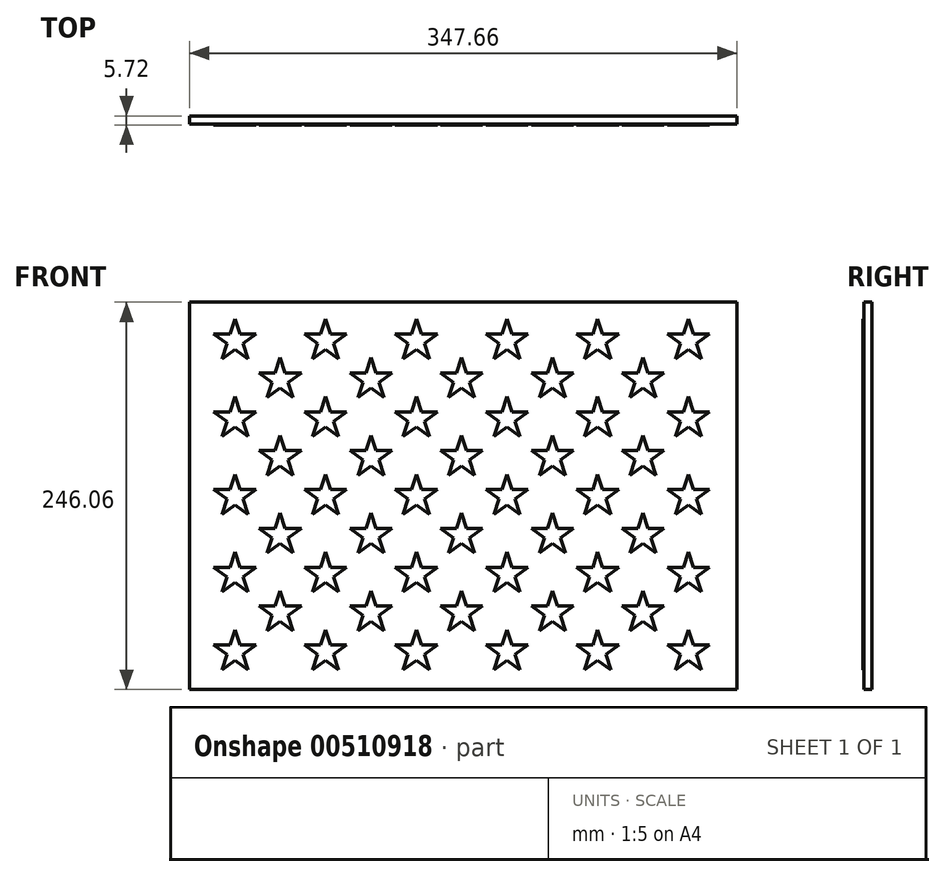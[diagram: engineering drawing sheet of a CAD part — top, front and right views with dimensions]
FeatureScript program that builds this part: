
annotation { "Feature Type Name" : "Feature", "Feature Type Description" : "" }
export const myFeature = defineFeature(function(context is Context, id is Id, definition is map)
    precondition{}
    {
        {
            var Q0;
            Q0=qCreatedBy(makeId("Front.planeOp"),FACE);
            var sketch = newSketch(context, id + "F0", { "sketchPlane" : qUnion([Q0])});
            skLineSegment(sketch, "E0.bottom", {"start": v(-168.64, 139.52) * mm, "end": v(179.02, 139.52) * mm});
            skLineSegment(sketch, "E0.top", {"start": v(-168.64, -106.54) * mm, "end": v(179.02, -106.54) * mm});
            skLineSegment(sketch, "E0.left", {"start": v(-168.64, 139.52) * mm, "end": v(-168.64, -106.54) * mm});
            skLineSegment(sketch, "E0.right", {"start": v(179.02, 139.52) * mm, "end": v(179.02, -106.54) * mm});
            skSolve(sketch);
        }
        {
            var Q0;
            Q0=makeQuery(id+"F0.imprint","IMPRINT",FACE,{"disambiguationData":[TD([[makeQuery(id+"F0.imprint","IMPRINT",EDGE,{"derivedFrom":sQuery(id+"F0.wireOp",EDGE,"E0.bottom")}),-1.0]])]});
            var sketch = newSketch(context, id + "F1", { "sketchPlane" : qUnion([Q0])});
            skCircle(sketch, "E1", {"center": v(-139.84, 114.83) * mm, "radius": 14.08 * mm});
            skCircle(sketch, "E2.1.0.0", {"center": v(-82.23, 114.83) * mm, "radius": 14.08 * mm});
            skLineSegment(sketch, "E2.direction1", {"start": v(-139.84, 114.83) * mm, "end": v(-82.23, 114.83) * mm, "construction": true});
            skCircle(sketch, "E3.0.1.0", {"center": v(-139.84, 65.45) * mm, "radius": 14.08 * mm});
            skCircle(sketch, "E3.0.2.0", {"center": v(-139.84, 16.08) * mm, "radius": 14.08 * mm});
            skCircle(sketch, "E3.0.3.0", {"center": v(-139.84, -33.3) * mm, "radius": 14.08 * mm});
            skCircle(sketch, "E3.0.4.0", {"center": v(-139.84, -82.68) * mm, "radius": 14.08 * mm});
            skCircle(sketch, "E3.1.1.0", {"center": v(-82.23, 65.45) * mm, "radius": 14.08 * mm});
            skCircle(sketch, "E3.1.2.0", {"center": v(-82.23, 16.08) * mm, "radius": 14.08 * mm});
            skCircle(sketch, "E3.1.3.0", {"center": v(-82.23, -33.3) * mm, "radius": 14.08 * mm});
            skCircle(sketch, "E3.1.4.0", {"center": v(-82.23, -82.68) * mm, "radius": 14.08 * mm});
            skCircle(sketch, "E3.2.1.0", {"center": v(-24.63, 65.45) * mm, "radius": 14.08 * mm});
            skCircle(sketch, "E3.2.2.0", {"center": v(-24.63, 16.08) * mm, "radius": 14.08 * mm});
            skCircle(sketch, "E3.2.3.0", {"center": v(-24.63, -33.3) * mm, "radius": 14.08 * mm});
            skCircle(sketch, "E3.2.4.0", {"center": v(-24.63, -82.68) * mm, "radius": 14.08 * mm});
            skCircle(sketch, "E3.3.0.0", {"center": v(32.98, 114.83) * mm, "radius": 14.08 * mm});
            skCircle(sketch, "E3.3.1.0", {"center": v(32.98, 65.45) * mm, "radius": 14.08 * mm});
            skCircle(sketch, "E3.3.2.0", {"center": v(32.98, 16.08) * mm, "radius": 14.08 * mm});
            skCircle(sketch, "E3.3.3.0", {"center": v(32.98, -33.3) * mm, "radius": 14.08 * mm});
            skCircle(sketch, "E3.3.4.0", {"center": v(32.98, -82.68) * mm, "radius": 14.08 * mm});
            skCircle(sketch, "E3.4.0.0", {"center": v(90.59, 114.83) * mm, "radius": 14.08 * mm});
            skCircle(sketch, "E3.4.1.0", {"center": v(90.59, 65.45) * mm, "radius": 14.08 * mm});
            skCircle(sketch, "E3.4.2.0", {"center": v(90.59, 16.08) * mm, "radius": 14.08 * mm});
            skCircle(sketch, "E3.4.3.0", {"center": v(90.59, -33.3) * mm, "radius": 14.08 * mm});
            skCircle(sketch, "E3.4.4.0", {"center": v(90.59, -82.68) * mm, "radius": 14.08 * mm});
            skCircle(sketch, "E3.5.0.0", {"center": v(148.2, 114.83) * mm, "radius": 14.08 * mm});
            skCircle(sketch, "E3.5.1.0", {"center": v(148.2, 65.45) * mm, "radius": 14.08 * mm});
            skCircle(sketch, "E3.5.2.0", {"center": v(148.2, 16.08) * mm, "radius": 14.08 * mm});
            skCircle(sketch, "E3.5.3.0", {"center": v(148.2, -33.3) * mm, "radius": 14.08 * mm});
            skCircle(sketch, "E3.5.4.0", {"center": v(148.2, -82.68) * mm, "radius": 14.08 * mm});
            skLineSegment(sketch, "E3.direction2", {"start": v(-139.84, 114.83) * mm, "end": v(-139.84, 65.45) * mm, "construction": true});
            skCircle(sketch, "E4.1.0.0", {"center": v(-24.63, 114.83) * mm, "radius": 14.08 * mm});
            skLineSegment(sketch, "E4.direction1", {"start": v(-82.23, 114.83) * mm, "end": v(-24.63, 114.83) * mm, "construction": true});
            skCircle(sketch, "E5", {"center": v(-111.04, 90.14) * mm, "radius": 14.08 * mm});
            skCircle(sketch, "E6.0.1.0", {"center": v(-111.04, 40.77) * mm, "radius": 14.08 * mm});
            skCircle(sketch, "E6.0.2.0", {"center": v(-111.04, -8.61) * mm, "radius": 14.08 * mm});
            skCircle(sketch, "E6.0.3.0", {"center": v(-111.04, -57.99) * mm, "radius": 14.08 * mm});
            skCircle(sketch, "E6.1.0.0", {"center": v(-53.43, 90.14) * mm, "radius": 14.08 * mm});
            skCircle(sketch, "E6.1.1.0", {"center": v(-53.43, 40.77) * mm, "radius": 14.08 * mm});
            skCircle(sketch, "E6.1.2.0", {"center": v(-53.43, -8.61) * mm, "radius": 14.08 * mm});
            skCircle(sketch, "E6.1.3.0", {"center": v(-53.43, -57.99) * mm, "radius": 14.08 * mm});
            skCircle(sketch, "E6.2.0.0", {"center": v(4.18, 90.14) * mm, "radius": 14.08 * mm});
            skCircle(sketch, "E6.2.1.0", {"center": v(4.18, 40.77) * mm, "radius": 14.08 * mm});
            skCircle(sketch, "E6.2.2.0", {"center": v(4.18, -8.61) * mm, "radius": 14.08 * mm});
            skCircle(sketch, "E6.2.3.0", {"center": v(4.18, -57.99) * mm, "radius": 14.08 * mm});
            skCircle(sketch, "E6.3.0.0", {"center": v(61.78, 90.14) * mm, "radius": 14.08 * mm});
            skCircle(sketch, "E6.3.1.0", {"center": v(61.78, 40.77) * mm, "radius": 14.08 * mm});
            skCircle(sketch, "E6.3.2.0", {"center": v(61.78, -8.61) * mm, "radius": 14.08 * mm});
            skCircle(sketch, "E6.3.3.0", {"center": v(61.78, -57.99) * mm, "radius": 14.08 * mm});
            skCircle(sketch, "E6.4.0.0", {"center": v(119.4, 90.14) * mm, "radius": 14.08 * mm});
            skCircle(sketch, "E6.4.1.0", {"center": v(119.4, 40.77) * mm, "radius": 14.08 * mm});
            skCircle(sketch, "E6.4.2.0", {"center": v(119.4, -8.61) * mm, "radius": 14.08 * mm});
            skCircle(sketch, "E6.4.3.0", {"center": v(119.4, -57.99) * mm, "radius": 14.08 * mm});
            skLineSegment(sketch, "E6.direction1", {"start": v(-111.04, 90.14) * mm, "end": v(-53.43, 90.14) * mm, "construction": true});
            skLineSegment(sketch, "E6.direction2", {"start": v(-111.04, 90.14) * mm, "end": v(-111.04, 40.77) * mm, "construction": true});
            skSolve(sketch);
        }
        {
            var Q0;
            Q0=makeQuery(id+"F0.imprint","IMPRINT",FACE,{"disambiguationData":[TD([[makeQuery(id+"F0.imprint","IMPRINT",EDGE,{"derivedFrom":sQuery(id+"F0.wireOp",EDGE,"E0.bottom")}),-1.0]])]});
            var sketch = newSketch(context, id + "F2", { "sketchPlane" : qUnion([Q0])});
            skLineSegment(sketch, "E7", {"start": v(-139.83, 128.91) * mm, "end": v(-143, 119.19) * mm});
            skLineSegment(sketch, "E8", {"start": v(-131.57, 103.43) * mm, "end": v(-134.73, 113.17) * mm});
            skLineSegment(sketch, "E9", {"start": v(-131.57, 103.43) * mm, "end": v(-139.84, 109.45) * mm});
            skLineSegment(sketch, "E10", {"start": v(-153.23, 119.2) * mm, "end": v(-143, 119.19) * mm});
            skLineSegment(sketch, "E11", {"start": v(-126.44, 119.17) * mm, "end": v(-134.73, 113.17) * mm});
            skLineSegment(sketch, "E12.trimOffspring", {"start": v(-144.96, 113.17) * mm, "end": v(-148.13, 103.45) * mm});
            skLineSegment(sketch, "E13.trimOffspring", {"start": v(-144.96, 113.17) * mm, "end": v(-153.23, 119.2) * mm});
            skLineSegment(sketch, "E14.trimOffspring", {"start": v(-139.84, 109.45) * mm, "end": v(-148.13, 103.45) * mm});
            skLineSegment(sketch, "E15.trimOffspring", {"start": v(-136.68, 119.18) * mm, "end": v(-139.83, 128.91) * mm});
            skLineSegment(sketch, "E16.trimOffspring", {"start": v(-136.68, 119.18) * mm, "end": v(-126.44, 119.17) * mm});
            skLineSegment(sketch, "E17.0.1.0", {"start": v(-144.96, 63.8) * mm, "end": v(-153.23, 69.82) * mm});
            skLineSegment(sketch, "E17.0.1.1", {"start": v(-136.68, 69.8) * mm, "end": v(-139.83, 79.54) * mm});
            skLineSegment(sketch, "E17.0.1.2", {"start": v(-139.83, 79.54) * mm, "end": v(-143, 69.8) * mm});
            skLineSegment(sketch, "E17.0.1.3", {"start": v(-139.84, 60.08) * mm, "end": v(-148.13, 54.07) * mm});
            skLineSegment(sketch, "E17.0.1.4", {"start": v(-131.57, 54.06) * mm, "end": v(-139.84, 60.08) * mm});
            skLineSegment(sketch, "E17.0.1.5", {"start": v(-144.96, 63.8) * mm, "end": v(-148.13, 54.07) * mm});
            skLineSegment(sketch, "E17.0.1.6", {"start": v(-126.44, 69.8) * mm, "end": v(-134.73, 63.79) * mm});
            skLineSegment(sketch, "E17.0.1.7", {"start": v(-136.68, 69.8) * mm, "end": v(-126.44, 69.8) * mm});
            skLineSegment(sketch, "E17.0.1.8", {"start": v(-153.23, 69.82) * mm, "end": v(-143, 69.8) * mm});
            skLineSegment(sketch, "E17.0.1.9", {"start": v(-131.57, 54.06) * mm, "end": v(-134.73, 63.79) * mm});
            skLineSegment(sketch, "E17.0.2.0", {"start": v(-144.96, 14.42) * mm, "end": v(-153.23, 20.44) * mm});
            skLineSegment(sketch, "E17.0.2.1", {"start": v(-136.68, 20.43) * mm, "end": v(-139.83, 30.16) * mm});
            skLineSegment(sketch, "E17.0.2.2", {"start": v(-139.83, 30.16) * mm, "end": v(-143, 20.43) * mm});
            skLineSegment(sketch, "E17.0.2.3", {"start": v(-139.84, 10.7) * mm, "end": v(-148.13, 4.7) * mm});
            skLineSegment(sketch, "E17.0.2.4", {"start": v(-131.57, 4.68) * mm, "end": v(-139.84, 10.7) * mm});
            skLineSegment(sketch, "E17.0.2.5", {"start": v(-144.96, 14.42) * mm, "end": v(-148.13, 4.7) * mm});
            skLineSegment(sketch, "E17.0.2.6", {"start": v(-126.44, 20.42) * mm, "end": v(-134.73, 14.41) * mm});
            skLineSegment(sketch, "E17.0.2.7", {"start": v(-136.68, 20.43) * mm, "end": v(-126.44, 20.42) * mm});
            skLineSegment(sketch, "E17.0.2.8", {"start": v(-153.23, 20.44) * mm, "end": v(-143, 20.43) * mm});
            skLineSegment(sketch, "E17.0.2.9", {"start": v(-131.57, 4.68) * mm, "end": v(-134.73, 14.41) * mm});
            skLineSegment(sketch, "E17.0.3.0", {"start": v(-144.96, -34.96) * mm, "end": v(-153.23, -28.94) * mm});
            skLineSegment(sketch, "E17.0.3.1", {"start": v(-136.68, -28.95) * mm, "end": v(-139.83, -19.22) * mm});
            skLineSegment(sketch, "E17.0.3.2", {"start": v(-139.83, -19.22) * mm, "end": v(-143, -28.95) * mm});
            skLineSegment(sketch, "E17.0.3.3", {"start": v(-139.84, -38.68) * mm, "end": v(-148.13, -44.69) * mm});
            skLineSegment(sketch, "E17.0.3.4", {"start": v(-131.57, -44.7) * mm, "end": v(-139.84, -38.68) * mm});
            skLineSegment(sketch, "E17.0.3.5", {"start": v(-144.96, -34.96) * mm, "end": v(-148.13, -44.69) * mm});
            skLineSegment(sketch, "E17.0.3.6", {"start": v(-126.44, -28.96) * mm, "end": v(-134.73, -34.97) * mm});
            skLineSegment(sketch, "E17.0.3.7", {"start": v(-136.68, -28.95) * mm, "end": v(-126.44, -28.96) * mm});
            skLineSegment(sketch, "E17.0.3.8", {"start": v(-153.23, -28.94) * mm, "end": v(-143, -28.95) * mm});
            skLineSegment(sketch, "E17.0.3.9", {"start": v(-131.57, -44.7) * mm, "end": v(-134.73, -34.97) * mm});
            skLineSegment(sketch, "E17.0.4.0", {"start": v(-144.96, -84.34) * mm, "end": v(-153.23, -78.32) * mm});
            skLineSegment(sketch, "E17.0.4.1", {"start": v(-136.68, -78.33) * mm, "end": v(-139.83, -68.6) * mm});
            skLineSegment(sketch, "E17.0.4.2", {"start": v(-139.83, -68.6) * mm, "end": v(-143, -78.32) * mm});
            skLineSegment(sketch, "E17.0.4.3", {"start": v(-139.84, -88.06) * mm, "end": v(-148.13, -94.06) * mm});
            skLineSegment(sketch, "E17.0.4.4", {"start": v(-131.57, -94.08) * mm, "end": v(-139.84, -88.06) * mm});
            skLineSegment(sketch, "E17.0.4.5", {"start": v(-144.96, -84.34) * mm, "end": v(-148.13, -94.06) * mm});
            skLineSegment(sketch, "E17.0.4.6", {"start": v(-126.44, -78.34) * mm, "end": v(-134.73, -84.34) * mm});
            skLineSegment(sketch, "E17.0.4.7", {"start": v(-136.68, -78.33) * mm, "end": v(-126.44, -78.34) * mm});
            skLineSegment(sketch, "E17.0.4.8", {"start": v(-153.23, -78.32) * mm, "end": v(-143, -78.32) * mm});
            skLineSegment(sketch, "E17.0.4.9", {"start": v(-131.57, -94.08) * mm, "end": v(-134.73, -84.34) * mm});
            skLineSegment(sketch, "E17.1.0.0", {"start": v(-87.35, 113.17) * mm, "end": v(-95.62, 119.2) * mm});
            skLineSegment(sketch, "E17.1.0.1", {"start": v(-79.07, 119.18) * mm, "end": v(-82.22, 128.91) * mm});
            skLineSegment(sketch, "E17.1.0.2", {"start": v(-82.22, 128.91) * mm, "end": v(-85.4, 119.19) * mm});
            skLineSegment(sketch, "E17.1.0.3", {"start": v(-82.24, 109.45) * mm, "end": v(-90.52, 103.45) * mm});
            skLineSegment(sketch, "E17.1.0.4", {"start": v(-73.97, 103.43) * mm, "end": v(-82.24, 109.45) * mm});
            skLineSegment(sketch, "E17.1.0.5", {"start": v(-87.35, 113.17) * mm, "end": v(-90.52, 103.45) * mm});
            skLineSegment(sketch, "E17.1.0.6", {"start": v(-68.84, 119.17) * mm, "end": v(-77.12, 113.17) * mm});
            skLineSegment(sketch, "E17.1.0.7", {"start": v(-79.07, 119.18) * mm, "end": v(-68.84, 119.17) * mm});
            skLineSegment(sketch, "E17.1.0.8", {"start": v(-95.62, 119.2) * mm, "end": v(-85.4, 119.19) * mm});
            skLineSegment(sketch, "E17.1.0.9", {"start": v(-73.97, 103.43) * mm, "end": v(-77.12, 113.17) * mm});
            skLineSegment(sketch, "E17.1.1.0", {"start": v(-87.35, 63.8) * mm, "end": v(-95.62, 69.82) * mm});
            skLineSegment(sketch, "E17.1.1.1", {"start": v(-79.07, 69.8) * mm, "end": v(-82.22, 79.54) * mm});
            skLineSegment(sketch, "E17.1.1.2", {"start": v(-82.22, 79.54) * mm, "end": v(-85.4, 69.8) * mm});
            skLineSegment(sketch, "E17.1.1.3", {"start": v(-82.24, 60.08) * mm, "end": v(-90.52, 54.07) * mm});
            skLineSegment(sketch, "E17.1.1.4", {"start": v(-73.97, 54.06) * mm, "end": v(-82.24, 60.08) * mm});
            skLineSegment(sketch, "E17.1.1.5", {"start": v(-87.35, 63.8) * mm, "end": v(-90.52, 54.07) * mm});
            skLineSegment(sketch, "E17.1.1.6", {"start": v(-68.84, 69.8) * mm, "end": v(-77.12, 63.79) * mm});
            skLineSegment(sketch, "E17.1.1.7", {"start": v(-79.07, 69.8) * mm, "end": v(-68.84, 69.8) * mm});
            skLineSegment(sketch, "E17.1.1.8", {"start": v(-95.62, 69.82) * mm, "end": v(-85.4, 69.8) * mm});
            skLineSegment(sketch, "E17.1.1.9", {"start": v(-73.97, 54.06) * mm, "end": v(-77.12, 63.79) * mm});
            skLineSegment(sketch, "E17.1.2.0", {"start": v(-87.35, 14.42) * mm, "end": v(-95.62, 20.44) * mm});
            skLineSegment(sketch, "E17.1.2.1", {"start": v(-79.07, 20.43) * mm, "end": v(-82.22, 30.16) * mm});
            skLineSegment(sketch, "E17.1.2.2", {"start": v(-82.22, 30.16) * mm, "end": v(-85.4, 20.43) * mm});
            skLineSegment(sketch, "E17.1.2.3", {"start": v(-82.24, 10.7) * mm, "end": v(-90.52, 4.7) * mm});
            skLineSegment(sketch, "E17.1.2.4", {"start": v(-73.97, 4.68) * mm, "end": v(-82.24, 10.7) * mm});
            skLineSegment(sketch, "E17.1.2.5", {"start": v(-87.35, 14.42) * mm, "end": v(-90.52, 4.7) * mm});
            skLineSegment(sketch, "E17.1.2.6", {"start": v(-68.84, 20.42) * mm, "end": v(-77.12, 14.41) * mm});
            skLineSegment(sketch, "E17.1.2.7", {"start": v(-79.07, 20.43) * mm, "end": v(-68.84, 20.42) * mm});
            skLineSegment(sketch, "E17.1.2.8", {"start": v(-95.62, 20.44) * mm, "end": v(-85.4, 20.43) * mm});
            skLineSegment(sketch, "E17.1.2.9", {"start": v(-73.97, 4.68) * mm, "end": v(-77.12, 14.41) * mm});
            skLineSegment(sketch, "E17.1.3.0", {"start": v(-87.35, -34.96) * mm, "end": v(-95.62, -28.94) * mm});
            skLineSegment(sketch, "E17.1.3.1", {"start": v(-79.07, -28.95) * mm, "end": v(-82.22, -19.22) * mm});
            skLineSegment(sketch, "E17.1.3.2", {"start": v(-82.22, -19.22) * mm, "end": v(-85.4, -28.95) * mm});
            skLineSegment(sketch, "E17.1.3.3", {"start": v(-82.24, -38.68) * mm, "end": v(-90.52, -44.69) * mm});
            skLineSegment(sketch, "E17.1.3.4", {"start": v(-73.97, -44.7) * mm, "end": v(-82.24, -38.68) * mm});
            skLineSegment(sketch, "E17.1.3.5", {"start": v(-87.35, -34.96) * mm, "end": v(-90.52, -44.69) * mm});
            skLineSegment(sketch, "E17.1.3.6", {"start": v(-68.84, -28.96) * mm, "end": v(-77.12, -34.97) * mm});
            skLineSegment(sketch, "E17.1.3.7", {"start": v(-79.07, -28.95) * mm, "end": v(-68.84, -28.96) * mm});
            skLineSegment(sketch, "E17.1.3.8", {"start": v(-95.62, -28.94) * mm, "end": v(-85.4, -28.95) * mm});
            skLineSegment(sketch, "E17.1.3.9", {"start": v(-73.97, -44.7) * mm, "end": v(-77.12, -34.97) * mm});
            skLineSegment(sketch, "E17.1.4.0", {"start": v(-87.35, -84.34) * mm, "end": v(-95.62, -78.32) * mm});
            skLineSegment(sketch, "E17.1.4.1", {"start": v(-79.07, -78.33) * mm, "end": v(-82.22, -68.6) * mm});
            skLineSegment(sketch, "E17.1.4.2", {"start": v(-82.22, -68.6) * mm, "end": v(-85.4, -78.32) * mm});
            skLineSegment(sketch, "E17.1.4.3", {"start": v(-82.24, -88.06) * mm, "end": v(-90.52, -94.06) * mm});
            skLineSegment(sketch, "E17.1.4.4", {"start": v(-73.97, -94.08) * mm, "end": v(-82.24, -88.06) * mm});
            skLineSegment(sketch, "E17.1.4.5", {"start": v(-87.35, -84.34) * mm, "end": v(-90.52, -94.06) * mm});
            skLineSegment(sketch, "E17.1.4.6", {"start": v(-68.84, -78.34) * mm, "end": v(-77.12, -84.34) * mm});
            skLineSegment(sketch, "E17.1.4.7", {"start": v(-79.07, -78.33) * mm, "end": v(-68.84, -78.34) * mm});
            skLineSegment(sketch, "E17.1.4.8", {"start": v(-95.62, -78.32) * mm, "end": v(-85.4, -78.32) * mm});
            skLineSegment(sketch, "E17.1.4.9", {"start": v(-73.97, -94.08) * mm, "end": v(-77.12, -84.34) * mm});
            skLineSegment(sketch, "E17.2.0.0", {"start": v(-29.74, 113.17) * mm, "end": v(-38.02, 119.2) * mm});
            skLineSegment(sketch, "E17.2.0.1", {"start": v(-21.46, 119.18) * mm, "end": v(-24.62, 128.91) * mm});
            skLineSegment(sketch, "E17.2.0.2", {"start": v(-24.62, 128.91) * mm, "end": v(-27.78, 119.19) * mm});
            skLineSegment(sketch, "E17.2.0.3", {"start": v(-24.63, 109.45) * mm, "end": v(-32.91, 103.45) * mm});
            skLineSegment(sketch, "E17.2.0.4", {"start": v(-16.36, 103.43) * mm, "end": v(-24.63, 109.45) * mm});
            skLineSegment(sketch, "E17.2.0.5", {"start": v(-29.74, 113.17) * mm, "end": v(-32.91, 103.45) * mm});
            skLineSegment(sketch, "E17.2.0.6", {"start": v(-11.23, 119.17) * mm, "end": v(-19.51, 113.17) * mm});
            skLineSegment(sketch, "E17.2.0.7", {"start": v(-21.46, 119.18) * mm, "end": v(-11.23, 119.17) * mm});
            skLineSegment(sketch, "E17.2.0.8", {"start": v(-38.02, 119.2) * mm, "end": v(-27.78, 119.19) * mm});
            skLineSegment(sketch, "E17.2.0.9", {"start": v(-16.36, 103.43) * mm, "end": v(-19.51, 113.17) * mm});
            skLineSegment(sketch, "E17.2.1.0", {"start": v(-29.74, 63.8) * mm, "end": v(-38.02, 69.82) * mm});
            skLineSegment(sketch, "E17.2.1.1", {"start": v(-21.46, 69.8) * mm, "end": v(-24.62, 79.54) * mm});
            skLineSegment(sketch, "E17.2.1.2", {"start": v(-24.62, 79.54) * mm, "end": v(-27.78, 69.8) * mm});
            skLineSegment(sketch, "E17.2.1.3", {"start": v(-24.63, 60.08) * mm, "end": v(-32.91, 54.07) * mm});
            skLineSegment(sketch, "E17.2.1.4", {"start": v(-16.36, 54.06) * mm, "end": v(-24.63, 60.08) * mm});
            skLineSegment(sketch, "E17.2.1.5", {"start": v(-29.74, 63.8) * mm, "end": v(-32.91, 54.07) * mm});
            skLineSegment(sketch, "E17.2.1.6", {"start": v(-11.23, 69.8) * mm, "end": v(-19.51, 63.79) * mm});
            skLineSegment(sketch, "E17.2.1.7", {"start": v(-21.46, 69.8) * mm, "end": v(-11.23, 69.8) * mm});
            skLineSegment(sketch, "E17.2.1.8", {"start": v(-38.02, 69.82) * mm, "end": v(-27.78, 69.8) * mm});
            skLineSegment(sketch, "E17.2.1.9", {"start": v(-16.36, 54.06) * mm, "end": v(-19.51, 63.79) * mm});
            skLineSegment(sketch, "E17.2.2.0", {"start": v(-29.74, 14.42) * mm, "end": v(-38.02, 20.44) * mm});
            skLineSegment(sketch, "E17.2.2.1", {"start": v(-21.46, 20.43) * mm, "end": v(-24.62, 30.16) * mm});
            skLineSegment(sketch, "E17.2.2.2", {"start": v(-24.62, 30.16) * mm, "end": v(-27.78, 20.43) * mm});
            skLineSegment(sketch, "E17.2.2.3", {"start": v(-24.63, 10.7) * mm, "end": v(-32.91, 4.7) * mm});
            skLineSegment(sketch, "E17.2.2.4", {"start": v(-16.36, 4.68) * mm, "end": v(-24.63, 10.7) * mm});
            skLineSegment(sketch, "E17.2.2.5", {"start": v(-29.74, 14.42) * mm, "end": v(-32.91, 4.7) * mm});
            skLineSegment(sketch, "E17.2.2.6", {"start": v(-11.23, 20.42) * mm, "end": v(-19.51, 14.41) * mm});
            skLineSegment(sketch, "E17.2.2.7", {"start": v(-21.46, 20.43) * mm, "end": v(-11.23, 20.42) * mm});
            skLineSegment(sketch, "E17.2.2.8", {"start": v(-38.02, 20.44) * mm, "end": v(-27.78, 20.43) * mm});
            skLineSegment(sketch, "E17.2.2.9", {"start": v(-16.36, 4.68) * mm, "end": v(-19.51, 14.41) * mm});
            skLineSegment(sketch, "E17.2.3.0", {"start": v(-29.74, -34.96) * mm, "end": v(-38.02, -28.94) * mm});
            skLineSegment(sketch, "E17.2.3.1", {"start": v(-21.46, -28.95) * mm, "end": v(-24.62, -19.22) * mm});
            skLineSegment(sketch, "E17.2.3.2", {"start": v(-24.62, -19.22) * mm, "end": v(-27.78, -28.95) * mm});
            skLineSegment(sketch, "E17.2.3.3", {"start": v(-24.63, -38.68) * mm, "end": v(-32.91, -44.69) * mm});
            skLineSegment(sketch, "E17.2.3.4", {"start": v(-16.36, -44.7) * mm, "end": v(-24.63, -38.68) * mm});
            skLineSegment(sketch, "E17.2.3.5", {"start": v(-29.74, -34.96) * mm, "end": v(-32.91, -44.69) * mm});
            skLineSegment(sketch, "E17.2.3.6", {"start": v(-11.23, -28.96) * mm, "end": v(-19.51, -34.97) * mm});
            skLineSegment(sketch, "E17.2.3.7", {"start": v(-21.46, -28.95) * mm, "end": v(-11.23, -28.96) * mm});
            skLineSegment(sketch, "E17.2.3.8", {"start": v(-38.02, -28.94) * mm, "end": v(-27.78, -28.95) * mm});
            skLineSegment(sketch, "E17.2.3.9", {"start": v(-16.36, -44.7) * mm, "end": v(-19.51, -34.97) * mm});
            skLineSegment(sketch, "E17.2.4.0", {"start": v(-29.74, -84.34) * mm, "end": v(-38.02, -78.32) * mm});
            skLineSegment(sketch, "E17.2.4.1", {"start": v(-21.46, -78.33) * mm, "end": v(-24.62, -68.6) * mm});
            skLineSegment(sketch, "E17.2.4.2", {"start": v(-24.62, -68.6) * mm, "end": v(-27.78, -78.32) * mm});
            skLineSegment(sketch, "E17.2.4.3", {"start": v(-24.63, -88.06) * mm, "end": v(-32.91, -94.06) * mm});
            skLineSegment(sketch, "E17.2.4.4", {"start": v(-16.36, -94.08) * mm, "end": v(-24.63, -88.06) * mm});
            skLineSegment(sketch, "E17.2.4.5", {"start": v(-29.74, -84.34) * mm, "end": v(-32.91, -94.06) * mm});
            skLineSegment(sketch, "E17.2.4.6", {"start": v(-11.23, -78.34) * mm, "end": v(-19.51, -84.34) * mm});
            skLineSegment(sketch, "E17.2.4.7", {"start": v(-21.46, -78.33) * mm, "end": v(-11.23, -78.34) * mm});
            skLineSegment(sketch, "E17.2.4.8", {"start": v(-38.02, -78.32) * mm, "end": v(-27.78, -78.32) * mm});
            skLineSegment(sketch, "E17.2.4.9", {"start": v(-16.36, -94.08) * mm, "end": v(-19.51, -84.34) * mm});
            skLineSegment(sketch, "E17.3.0.0", {"start": v(27.86, 113.17) * mm, "end": v(19.6, 119.2) * mm});
            skLineSegment(sketch, "E17.3.0.1", {"start": v(36.15, 119.18) * mm, "end": v(33, 128.91) * mm});
            skLineSegment(sketch, "E17.3.0.2", {"start": v(33, 128.91) * mm, "end": v(29.82, 119.19) * mm});
            skLineSegment(sketch, "E17.3.0.3", {"start": v(32.98, 109.45) * mm, "end": v(24.7, 103.45) * mm});
            skLineSegment(sketch, "E17.3.0.4", {"start": v(41.25, 103.43) * mm, "end": v(32.98, 109.45) * mm});
            skLineSegment(sketch, "E17.3.0.5", {"start": v(27.86, 113.17) * mm, "end": v(24.7, 103.45) * mm});
            skLineSegment(sketch, "E17.3.0.6", {"start": v(46.38, 119.17) * mm, "end": v(38.1, 113.17) * mm});
            skLineSegment(sketch, "E17.3.0.7", {"start": v(36.15, 119.18) * mm, "end": v(46.38, 119.17) * mm});
            skLineSegment(sketch, "E17.3.0.8", {"start": v(19.6, 119.2) * mm, "end": v(29.82, 119.19) * mm});
            skLineSegment(sketch, "E17.3.0.9", {"start": v(41.25, 103.43) * mm, "end": v(38.1, 113.17) * mm});
            skLineSegment(sketch, "E17.3.1.0", {"start": v(27.86, 63.8) * mm, "end": v(19.6, 69.82) * mm});
            skLineSegment(sketch, "E17.3.1.1", {"start": v(36.15, 69.8) * mm, "end": v(33, 79.54) * mm});
            skLineSegment(sketch, "E17.3.1.2", {"start": v(33, 79.54) * mm, "end": v(29.82, 69.8) * mm});
            skLineSegment(sketch, "E17.3.1.3", {"start": v(32.98, 60.08) * mm, "end": v(24.7, 54.07) * mm});
            skLineSegment(sketch, "E17.3.1.4", {"start": v(41.25, 54.06) * mm, "end": v(32.98, 60.08) * mm});
            skLineSegment(sketch, "E17.3.1.5", {"start": v(27.86, 63.8) * mm, "end": v(24.7, 54.07) * mm});
            skLineSegment(sketch, "E17.3.1.6", {"start": v(46.38, 69.8) * mm, "end": v(38.1, 63.79) * mm});
            skLineSegment(sketch, "E17.3.1.7", {"start": v(36.15, 69.8) * mm, "end": v(46.38, 69.8) * mm});
            skLineSegment(sketch, "E17.3.1.8", {"start": v(19.6, 69.82) * mm, "end": v(29.82, 69.8) * mm});
            skLineSegment(sketch, "E17.3.1.9", {"start": v(41.25, 54.06) * mm, "end": v(38.1, 63.79) * mm});
            skLineSegment(sketch, "E17.3.2.0", {"start": v(27.86, 14.42) * mm, "end": v(19.6, 20.44) * mm});
            skLineSegment(sketch, "E17.3.2.1", {"start": v(36.15, 20.43) * mm, "end": v(33, 30.16) * mm});
            skLineSegment(sketch, "E17.3.2.2", {"start": v(33, 30.16) * mm, "end": v(29.82, 20.43) * mm});
            skLineSegment(sketch, "E17.3.2.3", {"start": v(32.98, 10.7) * mm, "end": v(24.7, 4.7) * mm});
            skLineSegment(sketch, "E17.3.2.4", {"start": v(41.25, 4.68) * mm, "end": v(32.98, 10.7) * mm});
            skLineSegment(sketch, "E17.3.2.5", {"start": v(27.86, 14.42) * mm, "end": v(24.7, 4.7) * mm});
            skLineSegment(sketch, "E17.3.2.6", {"start": v(46.38, 20.42) * mm, "end": v(38.1, 14.41) * mm});
            skLineSegment(sketch, "E17.3.2.7", {"start": v(36.15, 20.43) * mm, "end": v(46.38, 20.42) * mm});
            skLineSegment(sketch, "E17.3.2.8", {"start": v(19.6, 20.44) * mm, "end": v(29.82, 20.43) * mm});
            skLineSegment(sketch, "E17.3.2.9", {"start": v(41.25, 4.68) * mm, "end": v(38.1, 14.41) * mm});
            skLineSegment(sketch, "E17.3.3.0", {"start": v(27.86, -34.96) * mm, "end": v(19.6, -28.94) * mm});
            skLineSegment(sketch, "E17.3.3.1", {"start": v(36.15, -28.95) * mm, "end": v(33, -19.22) * mm});
            skLineSegment(sketch, "E17.3.3.2", {"start": v(33, -19.22) * mm, "end": v(29.82, -28.95) * mm});
            skLineSegment(sketch, "E17.3.3.3", {"start": v(32.98, -38.68) * mm, "end": v(24.7, -44.69) * mm});
            skLineSegment(sketch, "E17.3.3.4", {"start": v(41.25, -44.7) * mm, "end": v(32.98, -38.68) * mm});
            skLineSegment(sketch, "E17.3.3.5", {"start": v(27.86, -34.96) * mm, "end": v(24.7, -44.69) * mm});
            skLineSegment(sketch, "E17.3.3.6", {"start": v(46.38, -28.96) * mm, "end": v(38.1, -34.97) * mm});
            skLineSegment(sketch, "E17.3.3.7", {"start": v(36.15, -28.95) * mm, "end": v(46.38, -28.96) * mm});
            skLineSegment(sketch, "E17.3.3.8", {"start": v(19.6, -28.94) * mm, "end": v(29.82, -28.95) * mm});
            skLineSegment(sketch, "E17.3.3.9", {"start": v(41.25, -44.7) * mm, "end": v(38.1, -34.97) * mm});
            skLineSegment(sketch, "E17.3.4.0", {"start": v(27.86, -84.34) * mm, "end": v(19.6, -78.32) * mm});
            skLineSegment(sketch, "E17.3.4.1", {"start": v(36.15, -78.33) * mm, "end": v(33, -68.6) * mm});
            skLineSegment(sketch, "E17.3.4.2", {"start": v(33, -68.6) * mm, "end": v(29.82, -78.32) * mm});
            skLineSegment(sketch, "E17.3.4.3", {"start": v(32.98, -88.06) * mm, "end": v(24.7, -94.06) * mm});
            skLineSegment(sketch, "E17.3.4.4", {"start": v(41.25, -94.08) * mm, "end": v(32.98, -88.06) * mm});
            skLineSegment(sketch, "E17.3.4.5", {"start": v(27.86, -84.34) * mm, "end": v(24.7, -94.06) * mm});
            skLineSegment(sketch, "E17.3.4.6", {"start": v(46.38, -78.34) * mm, "end": v(38.1, -84.34) * mm});
            skLineSegment(sketch, "E17.3.4.7", {"start": v(36.15, -78.33) * mm, "end": v(46.38, -78.34) * mm});
            skLineSegment(sketch, "E17.3.4.8", {"start": v(19.6, -78.32) * mm, "end": v(29.82, -78.32) * mm});
            skLineSegment(sketch, "E17.3.4.9", {"start": v(41.25, -94.08) * mm, "end": v(38.1, -84.34) * mm});
            skLineSegment(sketch, "E17.4.0.0", {"start": v(85.47, 113.17) * mm, "end": v(77.2, 119.2) * mm});
            skLineSegment(sketch, "E17.4.0.1", {"start": v(93.75, 119.18) * mm, "end": v(90.6, 128.91) * mm});
            skLineSegment(sketch, "E17.4.0.2", {"start": v(90.6, 128.91) * mm, "end": v(87.43, 119.19) * mm});
            skLineSegment(sketch, "E17.4.0.3", {"start": v(90.58, 109.45) * mm, "end": v(82.3, 103.45) * mm});
            skLineSegment(sketch, "E17.4.0.4", {"start": v(98.86, 103.43) * mm, "end": v(90.58, 109.45) * mm});
            skLineSegment(sketch, "E17.4.0.5", {"start": v(85.47, 113.17) * mm, "end": v(82.3, 103.45) * mm});
            skLineSegment(sketch, "E17.4.0.6", {"start": v(103.98, 119.17) * mm, "end": v(95.7, 113.17) * mm});
            skLineSegment(sketch, "E17.4.0.7", {"start": v(93.75, 119.18) * mm, "end": v(103.98, 119.17) * mm});
            skLineSegment(sketch, "E17.4.0.8", {"start": v(77.2, 119.2) * mm, "end": v(87.43, 119.19) * mm});
            skLineSegment(sketch, "E17.4.0.9", {"start": v(98.86, 103.43) * mm, "end": v(95.7, 113.17) * mm});
            skLineSegment(sketch, "E17.4.1.0", {"start": v(85.47, 63.8) * mm, "end": v(77.2, 69.82) * mm});
            skLineSegment(sketch, "E17.4.1.1", {"start": v(93.75, 69.8) * mm, "end": v(90.6, 79.54) * mm});
            skLineSegment(sketch, "E17.4.1.2", {"start": v(90.6, 79.54) * mm, "end": v(87.43, 69.8) * mm});
            skLineSegment(sketch, "E17.4.1.3", {"start": v(90.58, 60.08) * mm, "end": v(82.3, 54.07) * mm});
            skLineSegment(sketch, "E17.4.1.4", {"start": v(98.86, 54.06) * mm, "end": v(90.58, 60.08) * mm});
            skLineSegment(sketch, "E17.4.1.5", {"start": v(85.47, 63.8) * mm, "end": v(82.3, 54.07) * mm});
            skLineSegment(sketch, "E17.4.1.6", {"start": v(103.98, 69.8) * mm, "end": v(95.7, 63.79) * mm});
            skLineSegment(sketch, "E17.4.1.7", {"start": v(93.75, 69.8) * mm, "end": v(103.98, 69.8) * mm});
            skLineSegment(sketch, "E17.4.1.8", {"start": v(77.2, 69.82) * mm, "end": v(87.43, 69.8) * mm});
            skLineSegment(sketch, "E17.4.1.9", {"start": v(98.86, 54.06) * mm, "end": v(95.7, 63.79) * mm});
            skLineSegment(sketch, "E17.4.2.0", {"start": v(85.47, 14.42) * mm, "end": v(77.2, 20.44) * mm});
            skLineSegment(sketch, "E17.4.2.1", {"start": v(93.75, 20.43) * mm, "end": v(90.6, 30.16) * mm});
            skLineSegment(sketch, "E17.4.2.2", {"start": v(90.6, 30.16) * mm, "end": v(87.43, 20.43) * mm});
            skLineSegment(sketch, "E17.4.2.3", {"start": v(90.58, 10.7) * mm, "end": v(82.3, 4.7) * mm});
            skLineSegment(sketch, "E17.4.2.4", {"start": v(98.86, 4.68) * mm, "end": v(90.58, 10.7) * mm});
            skLineSegment(sketch, "E17.4.2.5", {"start": v(85.47, 14.42) * mm, "end": v(82.3, 4.7) * mm});
            skLineSegment(sketch, "E17.4.2.6", {"start": v(103.98, 20.42) * mm, "end": v(95.7, 14.41) * mm});
            skLineSegment(sketch, "E17.4.2.7", {"start": v(93.75, 20.43) * mm, "end": v(103.98, 20.42) * mm});
            skLineSegment(sketch, "E17.4.2.8", {"start": v(77.2, 20.44) * mm, "end": v(87.43, 20.43) * mm});
            skLineSegment(sketch, "E17.4.2.9", {"start": v(98.86, 4.68) * mm, "end": v(95.7, 14.41) * mm});
            skLineSegment(sketch, "E17.4.3.0", {"start": v(85.47, -34.96) * mm, "end": v(77.2, -28.94) * mm});
            skLineSegment(sketch, "E17.4.3.1", {"start": v(93.75, -28.95) * mm, "end": v(90.6, -19.22) * mm});
            skLineSegment(sketch, "E17.4.3.2", {"start": v(90.6, -19.22) * mm, "end": v(87.43, -28.95) * mm});
            skLineSegment(sketch, "E17.4.3.3", {"start": v(90.58, -38.68) * mm, "end": v(82.3, -44.69) * mm});
            skLineSegment(sketch, "E17.4.3.4", {"start": v(98.86, -44.7) * mm, "end": v(90.58, -38.68) * mm});
            skLineSegment(sketch, "E17.4.3.5", {"start": v(85.47, -34.96) * mm, "end": v(82.3, -44.69) * mm});
            skLineSegment(sketch, "E17.4.3.6", {"start": v(103.98, -28.96) * mm, "end": v(95.7, -34.97) * mm});
            skLineSegment(sketch, "E17.4.3.7", {"start": v(93.75, -28.95) * mm, "end": v(103.98, -28.96) * mm});
            skLineSegment(sketch, "E17.4.3.8", {"start": v(77.2, -28.94) * mm, "end": v(87.43, -28.95) * mm});
            skLineSegment(sketch, "E17.4.3.9", {"start": v(98.86, -44.7) * mm, "end": v(95.7, -34.97) * mm});
            skLineSegment(sketch, "E17.4.4.0", {"start": v(85.47, -84.34) * mm, "end": v(77.2, -78.32) * mm});
            skLineSegment(sketch, "E17.4.4.1", {"start": v(93.75, -78.33) * mm, "end": v(90.6, -68.6) * mm});
            skLineSegment(sketch, "E17.4.4.2", {"start": v(90.6, -68.6) * mm, "end": v(87.43, -78.32) * mm});
            skLineSegment(sketch, "E17.4.4.3", {"start": v(90.58, -88.06) * mm, "end": v(82.3, -94.06) * mm});
            skLineSegment(sketch, "E17.4.4.4", {"start": v(98.86, -94.08) * mm, "end": v(90.58, -88.06) * mm});
            skLineSegment(sketch, "E17.4.4.5", {"start": v(85.47, -84.34) * mm, "end": v(82.3, -94.06) * mm});
            skLineSegment(sketch, "E17.4.4.6", {"start": v(103.98, -78.34) * mm, "end": v(95.7, -84.34) * mm});
            skLineSegment(sketch, "E17.4.4.7", {"start": v(93.75, -78.33) * mm, "end": v(103.98, -78.34) * mm});
            skLineSegment(sketch, "E17.4.4.8", {"start": v(77.2, -78.32) * mm, "end": v(87.43, -78.32) * mm});
            skLineSegment(sketch, "E17.4.4.9", {"start": v(98.86, -94.08) * mm, "end": v(95.7, -84.34) * mm});
            skLineSegment(sketch, "E17.5.0.0", {"start": v(143.08, 113.17) * mm, "end": v(134.8, 119.2) * mm});
            skLineSegment(sketch, "E17.5.0.1", {"start": v(151.36, 119.18) * mm, "end": v(148.2, 128.91) * mm});
            skLineSegment(sketch, "E17.5.0.2", {"start": v(148.2, 128.91) * mm, "end": v(145.04, 119.19) * mm});
            skLineSegment(sketch, "E17.5.0.3", {"start": v(148.2, 109.45) * mm, "end": v(139.9, 103.45) * mm});
            skLineSegment(sketch, "E17.5.0.4", {"start": v(156.46, 103.43) * mm, "end": v(148.2, 109.45) * mm});
            skLineSegment(sketch, "E17.5.0.5", {"start": v(143.08, 113.17) * mm, "end": v(139.9, 103.45) * mm});
            skLineSegment(sketch, "E17.5.0.6", {"start": v(161.6, 119.17) * mm, "end": v(153.3, 113.17) * mm});
            skLineSegment(sketch, "E17.5.0.7", {"start": v(151.36, 119.18) * mm, "end": v(161.6, 119.17) * mm});
            skLineSegment(sketch, "E17.5.0.8", {"start": v(134.8, 119.2) * mm, "end": v(145.04, 119.19) * mm});
            skLineSegment(sketch, "E17.5.0.9", {"start": v(156.46, 103.43) * mm, "end": v(153.3, 113.17) * mm});
            skLineSegment(sketch, "E17.5.1.0", {"start": v(143.08, 63.8) * mm, "end": v(134.8, 69.82) * mm});
            skLineSegment(sketch, "E17.5.1.1", {"start": v(151.36, 69.8) * mm, "end": v(148.2, 79.54) * mm});
            skLineSegment(sketch, "E17.5.1.2", {"start": v(148.2, 79.54) * mm, "end": v(145.04, 69.8) * mm});
            skLineSegment(sketch, "E17.5.1.3", {"start": v(148.2, 60.08) * mm, "end": v(139.9, 54.07) * mm});
            skLineSegment(sketch, "E17.5.1.4", {"start": v(156.46, 54.06) * mm, "end": v(148.2, 60.08) * mm});
            skLineSegment(sketch, "E17.5.1.5", {"start": v(143.08, 63.8) * mm, "end": v(139.9, 54.07) * mm});
            skLineSegment(sketch, "E17.5.1.6", {"start": v(161.6, 69.8) * mm, "end": v(153.3, 63.79) * mm});
            skLineSegment(sketch, "E17.5.1.7", {"start": v(151.36, 69.8) * mm, "end": v(161.6, 69.8) * mm});
            skLineSegment(sketch, "E17.5.1.8", {"start": v(134.8, 69.82) * mm, "end": v(145.04, 69.8) * mm});
            skLineSegment(sketch, "E17.5.1.9", {"start": v(156.46, 54.06) * mm, "end": v(153.3, 63.79) * mm});
            skLineSegment(sketch, "E17.5.2.0", {"start": v(143.08, 14.42) * mm, "end": v(134.8, 20.44) * mm});
            skLineSegment(sketch, "E17.5.2.1", {"start": v(151.36, 20.43) * mm, "end": v(148.2, 30.16) * mm});
            skLineSegment(sketch, "E17.5.2.2", {"start": v(148.2, 30.16) * mm, "end": v(145.04, 20.43) * mm});
            skLineSegment(sketch, "E17.5.2.3", {"start": v(148.2, 10.7) * mm, "end": v(139.9, 4.7) * mm});
            skLineSegment(sketch, "E17.5.2.4", {"start": v(156.46, 4.68) * mm, "end": v(148.2, 10.7) * mm});
            skLineSegment(sketch, "E17.5.2.5", {"start": v(143.08, 14.42) * mm, "end": v(139.9, 4.7) * mm});
            skLineSegment(sketch, "E17.5.2.6", {"start": v(161.6, 20.42) * mm, "end": v(153.3, 14.41) * mm});
            skLineSegment(sketch, "E17.5.2.7", {"start": v(151.36, 20.43) * mm, "end": v(161.6, 20.42) * mm});
            skLineSegment(sketch, "E17.5.2.8", {"start": v(134.8, 20.44) * mm, "end": v(145.04, 20.43) * mm});
            skLineSegment(sketch, "E17.5.2.9", {"start": v(156.46, 4.68) * mm, "end": v(153.3, 14.41) * mm});
            skLineSegment(sketch, "E17.5.3.0", {"start": v(143.08, -34.96) * mm, "end": v(134.8, -28.94) * mm});
            skLineSegment(sketch, "E17.5.3.1", {"start": v(151.36, -28.95) * mm, "end": v(148.2, -19.22) * mm});
            skLineSegment(sketch, "E17.5.3.2", {"start": v(148.2, -19.22) * mm, "end": v(145.04, -28.95) * mm});
            skLineSegment(sketch, "E17.5.3.3", {"start": v(148.2, -38.68) * mm, "end": v(139.9, -44.69) * mm});
            skLineSegment(sketch, "E17.5.3.4", {"start": v(156.46, -44.7) * mm, "end": v(148.2, -38.68) * mm});
            skLineSegment(sketch, "E17.5.3.5", {"start": v(143.08, -34.96) * mm, "end": v(139.9, -44.69) * mm});
            skLineSegment(sketch, "E17.5.3.6", {"start": v(161.6, -28.96) * mm, "end": v(153.3, -34.97) * mm});
            skLineSegment(sketch, "E17.5.3.7", {"start": v(151.36, -28.95) * mm, "end": v(161.6, -28.96) * mm});
            skLineSegment(sketch, "E17.5.3.8", {"start": v(134.8, -28.94) * mm, "end": v(145.04, -28.95) * mm});
            skLineSegment(sketch, "E17.5.3.9", {"start": v(156.46, -44.7) * mm, "end": v(153.3, -34.97) * mm});
            skLineSegment(sketch, "E17.5.4.0", {"start": v(143.08, -84.34) * mm, "end": v(134.8, -78.32) * mm});
            skLineSegment(sketch, "E17.5.4.1", {"start": v(151.36, -78.33) * mm, "end": v(148.2, -68.6) * mm});
            skLineSegment(sketch, "E17.5.4.2", {"start": v(148.2, -68.6) * mm, "end": v(145.04, -78.32) * mm});
            skLineSegment(sketch, "E17.5.4.3", {"start": v(148.2, -88.06) * mm, "end": v(139.9, -94.06) * mm});
            skLineSegment(sketch, "E17.5.4.4", {"start": v(156.46, -94.08) * mm, "end": v(148.2, -88.06) * mm});
            skLineSegment(sketch, "E17.5.4.5", {"start": v(143.08, -84.34) * mm, "end": v(139.9, -94.06) * mm});
            skLineSegment(sketch, "E17.5.4.6", {"start": v(161.6, -78.34) * mm, "end": v(153.3, -84.34) * mm});
            skLineSegment(sketch, "E17.5.4.7", {"start": v(151.36, -78.33) * mm, "end": v(161.6, -78.34) * mm});
            skLineSegment(sketch, "E17.5.4.8", {"start": v(134.8, -78.32) * mm, "end": v(145.04, -78.32) * mm});
            skLineSegment(sketch, "E17.5.4.9", {"start": v(156.46, -94.08) * mm, "end": v(153.3, -84.34) * mm});
            skLineSegment(sketch, "E17.direction1", {"start": v(-148.13, 103.45) * mm, "end": v(-90.52, 103.45) * mm, "construction": true});
            skLineSegment(sketch, "E17.direction2", {"start": v(-148.13, 103.45) * mm, "end": v(-148.13, 54.07) * mm, "construction": true});
            skLineSegment(sketch, "E18", {"start": v(-111.04, 104.34) * mm, "end": v(-114.21, 94.62) * mm});
            skLineSegment(sketch, "E19", {"start": v(-102.78, 78.86) * mm, "end": v(-105.94, 88.6) * mm});
            skLineSegment(sketch, "E20", {"start": v(-102.78, 78.86) * mm, "end": v(-111.06, 84.88) * mm});
            skLineSegment(sketch, "E21", {"start": v(-124.44, 94.62) * mm, "end": v(-114.21, 94.62) * mm});
            skLineSegment(sketch, "E22", {"start": v(-97.66, 94.6) * mm, "end": v(-105.94, 88.6) * mm});
            skLineSegment(sketch, "E23.trimOffspring", {"start": v(-116.17, 88.6) * mm, "end": v(-119.34, 78.88) * mm});
            skLineSegment(sketch, "E24.trimOffspring", {"start": v(-116.17, 88.6) * mm, "end": v(-124.44, 94.62) * mm});
            skLineSegment(sketch, "E25.trimOffspring", {"start": v(-111.06, 84.88) * mm, "end": v(-119.34, 78.88) * mm});
            skLineSegment(sketch, "E26.trimOffspring", {"start": v(-107.89, 94.61) * mm, "end": v(-111.04, 104.34) * mm});
            skLineSegment(sketch, "E27.trimOffspring", {"start": v(-107.89, 94.61) * mm, "end": v(-97.66, 94.6) * mm});
            skLineSegment(sketch, "E28.0.1.0", {"start": v(-111.04, 54.97) * mm, "end": v(-114.21, 45.24) * mm});
            skLineSegment(sketch, "E28.0.1.1", {"start": v(-102.78, 29.49) * mm, "end": v(-105.94, 39.22) * mm});
            skLineSegment(sketch, "E28.0.1.2", {"start": v(-102.78, 29.49) * mm, "end": v(-111.06, 35.5) * mm});
            skLineSegment(sketch, "E28.0.1.3", {"start": v(-124.44, 45.25) * mm, "end": v(-114.21, 45.24) * mm});
            skLineSegment(sketch, "E28.0.1.4", {"start": v(-97.66, 45.23) * mm, "end": v(-105.94, 39.22) * mm});
            skLineSegment(sketch, "E28.0.1.5", {"start": v(-116.17, 39.23) * mm, "end": v(-119.34, 29.5) * mm});
            skLineSegment(sketch, "E28.0.1.6", {"start": v(-116.17, 39.23) * mm, "end": v(-124.44, 45.25) * mm});
            skLineSegment(sketch, "E28.0.1.7", {"start": v(-111.06, 35.5) * mm, "end": v(-119.34, 29.5) * mm});
            skLineSegment(sketch, "E28.0.1.8", {"start": v(-107.89, 45.23) * mm, "end": v(-111.04, 54.97) * mm});
            skLineSegment(sketch, "E28.0.1.9", {"start": v(-107.89, 45.23) * mm, "end": v(-97.66, 45.23) * mm});
            skLineSegment(sketch, "E28.0.2.0", {"start": v(-111.04, 5.59) * mm, "end": v(-114.21, -4.14) * mm});
            skLineSegment(sketch, "E28.0.2.1", {"start": v(-102.78, -19.9) * mm, "end": v(-105.94, -10.16) * mm});
            skLineSegment(sketch, "E28.0.2.2", {"start": v(-102.78, -19.9) * mm, "end": v(-111.06, -13.87) * mm});
            skLineSegment(sketch, "E28.0.2.3", {"start": v(-124.44, -4.13) * mm, "end": v(-114.21, -4.14) * mm});
            skLineSegment(sketch, "E28.0.2.4", {"start": v(-97.66, -4.15) * mm, "end": v(-105.94, -10.16) * mm});
            skLineSegment(sketch, "E28.0.2.5", {"start": v(-116.17, -10.15) * mm, "end": v(-119.34, -19.88) * mm});
            skLineSegment(sketch, "E28.0.2.6", {"start": v(-116.17, -10.15) * mm, "end": v(-124.44, -4.13) * mm});
            skLineSegment(sketch, "E28.0.2.7", {"start": v(-111.06, -13.87) * mm, "end": v(-119.34, -19.88) * mm});
            skLineSegment(sketch, "E28.0.2.8", {"start": v(-107.89, -4.14) * mm, "end": v(-111.04, 5.59) * mm});
            skLineSegment(sketch, "E28.0.2.9", {"start": v(-107.89, -4.14) * mm, "end": v(-97.66, -4.15) * mm});
            skLineSegment(sketch, "E28.0.3.0", {"start": v(-111.04, -43.79) * mm, "end": v(-114.21, -53.52) * mm});
            skLineSegment(sketch, "E28.0.3.1", {"start": v(-102.78, -69.27) * mm, "end": v(-105.94, -59.54) * mm});
            skLineSegment(sketch, "E28.0.3.2", {"start": v(-102.78, -69.27) * mm, "end": v(-111.06, -63.25) * mm});
            skLineSegment(sketch, "E28.0.3.3", {"start": v(-124.44, -53.5) * mm, "end": v(-114.21, -53.52) * mm});
            skLineSegment(sketch, "E28.0.3.4", {"start": v(-97.66, -53.53) * mm, "end": v(-105.94, -59.54) * mm});
            skLineSegment(sketch, "E28.0.3.5", {"start": v(-116.17, -59.53) * mm, "end": v(-119.34, -69.26) * mm});
            skLineSegment(sketch, "E28.0.3.6", {"start": v(-116.17, -59.53) * mm, "end": v(-124.44, -53.5) * mm});
            skLineSegment(sketch, "E28.0.3.7", {"start": v(-111.06, -63.25) * mm, "end": v(-119.34, -69.26) * mm});
            skLineSegment(sketch, "E28.0.3.8", {"start": v(-107.89, -53.52) * mm, "end": v(-111.04, -43.79) * mm});
            skLineSegment(sketch, "E28.0.3.9", {"start": v(-107.89, -53.52) * mm, "end": v(-97.66, -53.53) * mm});
            skLineSegment(sketch, "E28.1.0.0", {"start": v(-53.43, 104.34) * mm, "end": v(-56.6, 94.62) * mm});
            skLineSegment(sketch, "E28.1.0.1", {"start": v(-45.18, 78.86) * mm, "end": v(-48.33, 88.6) * mm});
            skLineSegment(sketch, "E28.1.0.2", {"start": v(-45.18, 78.86) * mm, "end": v(-53.45, 84.88) * mm});
            skLineSegment(sketch, "E28.1.0.3", {"start": v(-66.83, 94.62) * mm, "end": v(-56.6, 94.62) * mm});
            skLineSegment(sketch, "E28.1.0.4", {"start": v(-40.05, 94.6) * mm, "end": v(-48.33, 88.6) * mm});
            skLineSegment(sketch, "E28.1.0.5", {"start": v(-58.56, 88.6) * mm, "end": v(-61.73, 78.88) * mm});
            skLineSegment(sketch, "E28.1.0.6", {"start": v(-58.56, 88.6) * mm, "end": v(-66.83, 94.62) * mm});
            skLineSegment(sketch, "E28.1.0.7", {"start": v(-53.45, 84.88) * mm, "end": v(-61.73, 78.88) * mm});
            skLineSegment(sketch, "E28.1.0.8", {"start": v(-50.28, 94.61) * mm, "end": v(-53.43, 104.34) * mm});
            skLineSegment(sketch, "E28.1.0.9", {"start": v(-50.28, 94.61) * mm, "end": v(-40.05, 94.6) * mm});
            skLineSegment(sketch, "E28.1.1.0", {"start": v(-53.43, 54.97) * mm, "end": v(-56.6, 45.24) * mm});
            skLineSegment(sketch, "E28.1.1.1", {"start": v(-45.18, 29.49) * mm, "end": v(-48.33, 39.22) * mm});
            skLineSegment(sketch, "E28.1.1.2", {"start": v(-45.18, 29.49) * mm, "end": v(-53.45, 35.5) * mm});
            skLineSegment(sketch, "E28.1.1.3", {"start": v(-66.83, 45.25) * mm, "end": v(-56.6, 45.24) * mm});
            skLineSegment(sketch, "E28.1.1.4", {"start": v(-40.05, 45.23) * mm, "end": v(-48.33, 39.22) * mm});
            skLineSegment(sketch, "E28.1.1.5", {"start": v(-58.56, 39.23) * mm, "end": v(-61.73, 29.5) * mm});
            skLineSegment(sketch, "E28.1.1.6", {"start": v(-58.56, 39.23) * mm, "end": v(-66.83, 45.25) * mm});
            skLineSegment(sketch, "E28.1.1.7", {"start": v(-53.45, 35.5) * mm, "end": v(-61.73, 29.5) * mm});
            skLineSegment(sketch, "E28.1.1.8", {"start": v(-50.28, 45.23) * mm, "end": v(-53.43, 54.97) * mm});
            skLineSegment(sketch, "E28.1.1.9", {"start": v(-50.28, 45.23) * mm, "end": v(-40.05, 45.23) * mm});
            skLineSegment(sketch, "E28.1.2.0", {"start": v(-53.43, 5.59) * mm, "end": v(-56.6, -4.14) * mm});
            skLineSegment(sketch, "E28.1.2.1", {"start": v(-45.18, -19.9) * mm, "end": v(-48.33, -10.16) * mm});
            skLineSegment(sketch, "E28.1.2.2", {"start": v(-45.18, -19.9) * mm, "end": v(-53.45, -13.87) * mm});
            skLineSegment(sketch, "E28.1.2.3", {"start": v(-66.83, -4.13) * mm, "end": v(-56.6, -4.14) * mm});
            skLineSegment(sketch, "E28.1.2.4", {"start": v(-40.05, -4.15) * mm, "end": v(-48.33, -10.16) * mm});
            skLineSegment(sketch, "E28.1.2.5", {"start": v(-58.56, -10.15) * mm, "end": v(-61.73, -19.88) * mm});
            skLineSegment(sketch, "E28.1.2.6", {"start": v(-58.56, -10.15) * mm, "end": v(-66.83, -4.13) * mm});
            skLineSegment(sketch, "E28.1.2.7", {"start": v(-53.45, -13.87) * mm, "end": v(-61.73, -19.88) * mm});
            skLineSegment(sketch, "E28.1.2.8", {"start": v(-50.28, -4.14) * mm, "end": v(-53.43, 5.59) * mm});
            skLineSegment(sketch, "E28.1.2.9", {"start": v(-50.28, -4.14) * mm, "end": v(-40.05, -4.15) * mm});
            skLineSegment(sketch, "E28.1.3.0", {"start": v(-53.43, -43.79) * mm, "end": v(-56.6, -53.52) * mm});
            skLineSegment(sketch, "E28.1.3.1", {"start": v(-45.18, -69.27) * mm, "end": v(-48.33, -59.54) * mm});
            skLineSegment(sketch, "E28.1.3.2", {"start": v(-45.18, -69.27) * mm, "end": v(-53.45, -63.25) * mm});
            skLineSegment(sketch, "E28.1.3.3", {"start": v(-66.83, -53.5) * mm, "end": v(-56.6, -53.52) * mm});
            skLineSegment(sketch, "E28.1.3.4", {"start": v(-40.05, -53.53) * mm, "end": v(-48.33, -59.54) * mm});
            skLineSegment(sketch, "E28.1.3.5", {"start": v(-58.56, -59.53) * mm, "end": v(-61.73, -69.26) * mm});
            skLineSegment(sketch, "E28.1.3.6", {"start": v(-58.56, -59.53) * mm, "end": v(-66.83, -53.5) * mm});
            skLineSegment(sketch, "E28.1.3.7", {"start": v(-53.45, -63.25) * mm, "end": v(-61.73, -69.26) * mm});
            skLineSegment(sketch, "E28.1.3.8", {"start": v(-50.28, -53.52) * mm, "end": v(-53.43, -43.79) * mm});
            skLineSegment(sketch, "E28.1.3.9", {"start": v(-50.28, -53.52) * mm, "end": v(-40.05, -53.53) * mm});
            skLineSegment(sketch, "E28.2.0.0", {"start": v(4.17, 104.34) * mm, "end": v(1, 94.62) * mm});
            skLineSegment(sketch, "E28.2.0.1", {"start": v(12.43, 78.86) * mm, "end": v(9.28, 88.6) * mm});
            skLineSegment(sketch, "E28.2.0.2", {"start": v(12.43, 78.86) * mm, "end": v(4.16, 84.88) * mm});
            skLineSegment(sketch, "E28.2.0.3", {"start": v(-9.23, 94.62) * mm, "end": v(1, 94.62) * mm});
            skLineSegment(sketch, "E28.2.0.4", {"start": v(17.56, 94.6) * mm, "end": v(9.28, 88.6) * mm});
            skLineSegment(sketch, "E28.2.0.5", {"start": v(-0.95, 88.6) * mm, "end": v(-4.12, 78.88) * mm});
            skLineSegment(sketch, "E28.2.0.6", {"start": v(-0.95, 88.6) * mm, "end": v(-9.23, 94.62) * mm});
            skLineSegment(sketch, "E28.2.0.7", {"start": v(4.16, 84.88) * mm, "end": v(-4.12, 78.88) * mm});
            skLineSegment(sketch, "E28.2.0.8", {"start": v(7.33, 94.61) * mm, "end": v(4.17, 104.34) * mm});
            skLineSegment(sketch, "E28.2.0.9", {"start": v(7.33, 94.61) * mm, "end": v(17.56, 94.6) * mm});
            skLineSegment(sketch, "E28.2.1.0", {"start": v(4.17, 54.97) * mm, "end": v(1, 45.24) * mm});
            skLineSegment(sketch, "E28.2.1.1", {"start": v(12.43, 29.49) * mm, "end": v(9.28, 39.22) * mm});
            skLineSegment(sketch, "E28.2.1.2", {"start": v(12.43, 29.49) * mm, "end": v(4.16, 35.5) * mm});
            skLineSegment(sketch, "E28.2.1.3", {"start": v(-9.23, 45.25) * mm, "end": v(1, 45.24) * mm});
            skLineSegment(sketch, "E28.2.1.4", {"start": v(17.56, 45.23) * mm, "end": v(9.28, 39.22) * mm});
            skLineSegment(sketch, "E28.2.1.5", {"start": v(-0.95, 39.23) * mm, "end": v(-4.12, 29.5) * mm});
            skLineSegment(sketch, "E28.2.1.6", {"start": v(-0.95, 39.23) * mm, "end": v(-9.23, 45.25) * mm});
            skLineSegment(sketch, "E28.2.1.7", {"start": v(4.16, 35.5) * mm, "end": v(-4.12, 29.5) * mm});
            skLineSegment(sketch, "E28.2.1.8", {"start": v(7.33, 45.23) * mm, "end": v(4.17, 54.97) * mm});
            skLineSegment(sketch, "E28.2.1.9", {"start": v(7.33, 45.23) * mm, "end": v(17.56, 45.23) * mm});
            skLineSegment(sketch, "E28.2.2.0", {"start": v(4.17, 5.59) * mm, "end": v(1, -4.14) * mm});
            skLineSegment(sketch, "E28.2.2.1", {"start": v(12.43, -19.9) * mm, "end": v(9.28, -10.16) * mm});
            skLineSegment(sketch, "E28.2.2.2", {"start": v(12.43, -19.9) * mm, "end": v(4.16, -13.87) * mm});
            skLineSegment(sketch, "E28.2.2.3", {"start": v(-9.23, -4.13) * mm, "end": v(1, -4.14) * mm});
            skLineSegment(sketch, "E28.2.2.4", {"start": v(17.56, -4.15) * mm, "end": v(9.28, -10.16) * mm});
            skLineSegment(sketch, "E28.2.2.5", {"start": v(-0.95, -10.15) * mm, "end": v(-4.12, -19.88) * mm});
            skLineSegment(sketch, "E28.2.2.6", {"start": v(-0.95, -10.15) * mm, "end": v(-9.23, -4.13) * mm});
            skLineSegment(sketch, "E28.2.2.7", {"start": v(4.16, -13.87) * mm, "end": v(-4.12, -19.88) * mm});
            skLineSegment(sketch, "E28.2.2.8", {"start": v(7.33, -4.14) * mm, "end": v(4.17, 5.59) * mm});
            skLineSegment(sketch, "E28.2.2.9", {"start": v(7.33, -4.14) * mm, "end": v(17.56, -4.15) * mm});
            skLineSegment(sketch, "E28.2.3.0", {"start": v(4.17, -43.79) * mm, "end": v(1, -53.52) * mm});
            skLineSegment(sketch, "E28.2.3.1", {"start": v(12.43, -69.27) * mm, "end": v(9.28, -59.54) * mm});
            skLineSegment(sketch, "E28.2.3.2", {"start": v(12.43, -69.27) * mm, "end": v(4.16, -63.25) * mm});
            skLineSegment(sketch, "E28.2.3.3", {"start": v(-9.23, -53.5) * mm, "end": v(1, -53.52) * mm});
            skLineSegment(sketch, "E28.2.3.4", {"start": v(17.56, -53.53) * mm, "end": v(9.28, -59.54) * mm});
            skLineSegment(sketch, "E28.2.3.5", {"start": v(-0.95, -59.53) * mm, "end": v(-4.12, -69.26) * mm});
            skLineSegment(sketch, "E28.2.3.6", {"start": v(-0.95, -59.53) * mm, "end": v(-9.23, -53.5) * mm});
            skLineSegment(sketch, "E28.2.3.7", {"start": v(4.16, -63.25) * mm, "end": v(-4.12, -69.26) * mm});
            skLineSegment(sketch, "E28.2.3.8", {"start": v(7.33, -53.52) * mm, "end": v(4.17, -43.79) * mm});
            skLineSegment(sketch, "E28.2.3.9", {"start": v(7.33, -53.52) * mm, "end": v(17.56, -53.53) * mm});
            skLineSegment(sketch, "E28.3.0.0", {"start": v(61.78, 104.34) * mm, "end": v(58.61, 94.62) * mm});
            skLineSegment(sketch, "E28.3.0.1", {"start": v(70.04, 78.86) * mm, "end": v(66.88, 88.6) * mm});
            skLineSegment(sketch, "E28.3.0.2", {"start": v(70.04, 78.86) * mm, "end": v(61.77, 84.88) * mm});
            skLineSegment(sketch, "E28.3.0.3", {"start": v(48.38, 94.62) * mm, "end": v(58.61, 94.62) * mm});
            skLineSegment(sketch, "E28.3.0.4", {"start": v(75.17, 94.6) * mm, "end": v(66.88, 88.6) * mm});
            skLineSegment(sketch, "E28.3.0.5", {"start": v(56.65, 88.6) * mm, "end": v(53.48, 78.88) * mm});
            skLineSegment(sketch, "E28.3.0.6", {"start": v(56.65, 88.6) * mm, "end": v(48.38, 94.62) * mm});
            skLineSegment(sketch, "E28.3.0.7", {"start": v(61.77, 84.88) * mm, "end": v(53.48, 78.88) * mm});
            skLineSegment(sketch, "E28.3.0.8", {"start": v(64.93, 94.61) * mm, "end": v(61.78, 104.34) * mm});
            skLineSegment(sketch, "E28.3.0.9", {"start": v(64.93, 94.61) * mm, "end": v(75.17, 94.6) * mm});
            skLineSegment(sketch, "E28.3.1.0", {"start": v(61.78, 54.97) * mm, "end": v(58.61, 45.24) * mm});
            skLineSegment(sketch, "E28.3.1.1", {"start": v(70.04, 29.49) * mm, "end": v(66.88, 39.22) * mm});
            skLineSegment(sketch, "E28.3.1.2", {"start": v(70.04, 29.49) * mm, "end": v(61.77, 35.5) * mm});
            skLineSegment(sketch, "E28.3.1.3", {"start": v(48.38, 45.25) * mm, "end": v(58.61, 45.24) * mm});
            skLineSegment(sketch, "E28.3.1.4", {"start": v(75.17, 45.23) * mm, "end": v(66.88, 39.22) * mm});
            skLineSegment(sketch, "E28.3.1.5", {"start": v(56.65, 39.23) * mm, "end": v(53.48, 29.5) * mm});
            skLineSegment(sketch, "E28.3.1.6", {"start": v(56.65, 39.23) * mm, "end": v(48.38, 45.25) * mm});
            skLineSegment(sketch, "E28.3.1.7", {"start": v(61.77, 35.5) * mm, "end": v(53.48, 29.5) * mm});
            skLineSegment(sketch, "E28.3.1.8", {"start": v(64.93, 45.23) * mm, "end": v(61.78, 54.97) * mm});
            skLineSegment(sketch, "E28.3.1.9", {"start": v(64.93, 45.23) * mm, "end": v(75.17, 45.23) * mm});
            skLineSegment(sketch, "E28.3.2.0", {"start": v(61.78, 5.59) * mm, "end": v(58.61, -4.14) * mm});
            skLineSegment(sketch, "E28.3.2.1", {"start": v(70.04, -19.9) * mm, "end": v(66.88, -10.16) * mm});
            skLineSegment(sketch, "E28.3.2.2", {"start": v(70.04, -19.9) * mm, "end": v(61.77, -13.87) * mm});
            skLineSegment(sketch, "E28.3.2.3", {"start": v(48.38, -4.13) * mm, "end": v(58.61, -4.14) * mm});
            skLineSegment(sketch, "E28.3.2.4", {"start": v(75.17, -4.15) * mm, "end": v(66.88, -10.16) * mm});
            skLineSegment(sketch, "E28.3.2.5", {"start": v(56.65, -10.15) * mm, "end": v(53.48, -19.88) * mm});
            skLineSegment(sketch, "E28.3.2.6", {"start": v(56.65, -10.15) * mm, "end": v(48.38, -4.13) * mm});
            skLineSegment(sketch, "E28.3.2.7", {"start": v(61.77, -13.87) * mm, "end": v(53.48, -19.88) * mm});
            skLineSegment(sketch, "E28.3.2.8", {"start": v(64.93, -4.14) * mm, "end": v(61.78, 5.59) * mm});
            skLineSegment(sketch, "E28.3.2.9", {"start": v(64.93, -4.14) * mm, "end": v(75.17, -4.15) * mm});
            skLineSegment(sketch, "E28.3.3.0", {"start": v(61.78, -43.79) * mm, "end": v(58.61, -53.52) * mm});
            skLineSegment(sketch, "E28.3.3.1", {"start": v(70.04, -69.27) * mm, "end": v(66.88, -59.54) * mm});
            skLineSegment(sketch, "E28.3.3.2", {"start": v(70.04, -69.27) * mm, "end": v(61.77, -63.25) * mm});
            skLineSegment(sketch, "E28.3.3.3", {"start": v(48.38, -53.5) * mm, "end": v(58.61, -53.52) * mm});
            skLineSegment(sketch, "E28.3.3.4", {"start": v(75.17, -53.53) * mm, "end": v(66.88, -59.54) * mm});
            skLineSegment(sketch, "E28.3.3.5", {"start": v(56.65, -59.53) * mm, "end": v(53.48, -69.26) * mm});
            skLineSegment(sketch, "E28.3.3.6", {"start": v(56.65, -59.53) * mm, "end": v(48.38, -53.5) * mm});
            skLineSegment(sketch, "E28.3.3.7", {"start": v(61.77, -63.25) * mm, "end": v(53.48, -69.26) * mm});
            skLineSegment(sketch, "E28.3.3.8", {"start": v(64.93, -53.52) * mm, "end": v(61.78, -43.79) * mm});
            skLineSegment(sketch, "E28.3.3.9", {"start": v(64.93, -53.52) * mm, "end": v(75.17, -53.53) * mm});
            skLineSegment(sketch, "E28.4.0.0", {"start": v(119.39, 104.34) * mm, "end": v(116.22, 94.62) * mm});
            skLineSegment(sketch, "E28.4.0.1", {"start": v(127.64, 78.86) * mm, "end": v(124.5, 88.6) * mm});
            skLineSegment(sketch, "E28.4.0.2", {"start": v(127.64, 78.86) * mm, "end": v(119.37, 84.88) * mm});
            skLineSegment(sketch, "E28.4.0.3", {"start": v(105.99, 94.62) * mm, "end": v(116.22, 94.62) * mm});
            skLineSegment(sketch, "E28.4.0.4", {"start": v(132.77, 94.6) * mm, "end": v(124.5, 88.6) * mm});
            skLineSegment(sketch, "E28.4.0.5", {"start": v(114.26, 88.6) * mm, "end": v(111.1, 78.88) * mm});
            skLineSegment(sketch, "E28.4.0.6", {"start": v(114.26, 88.6) * mm, "end": v(105.99, 94.62) * mm});
            skLineSegment(sketch, "E28.4.0.7", {"start": v(119.37, 84.88) * mm, "end": v(111.1, 78.88) * mm});
            skLineSegment(sketch, "E28.4.0.8", {"start": v(122.54, 94.61) * mm, "end": v(119.39, 104.34) * mm});
            skLineSegment(sketch, "E28.4.0.9", {"start": v(122.54, 94.61) * mm, "end": v(132.77, 94.6) * mm});
            skLineSegment(sketch, "E28.4.1.0", {"start": v(119.39, 54.97) * mm, "end": v(116.22, 45.24) * mm});
            skLineSegment(sketch, "E28.4.1.1", {"start": v(127.64, 29.49) * mm, "end": v(124.5, 39.22) * mm});
            skLineSegment(sketch, "E28.4.1.2", {"start": v(127.64, 29.49) * mm, "end": v(119.37, 35.5) * mm});
            skLineSegment(sketch, "E28.4.1.3", {"start": v(105.99, 45.25) * mm, "end": v(116.22, 45.24) * mm});
            skLineSegment(sketch, "E28.4.1.4", {"start": v(132.77, 45.23) * mm, "end": v(124.5, 39.22) * mm});
            skLineSegment(sketch, "E28.4.1.5", {"start": v(114.26, 39.23) * mm, "end": v(111.1, 29.5) * mm});
            skLineSegment(sketch, "E28.4.1.6", {"start": v(114.26, 39.23) * mm, "end": v(105.99, 45.25) * mm});
            skLineSegment(sketch, "E28.4.1.7", {"start": v(119.37, 35.5) * mm, "end": v(111.1, 29.5) * mm});
            skLineSegment(sketch, "E28.4.1.8", {"start": v(122.54, 45.23) * mm, "end": v(119.39, 54.97) * mm});
            skLineSegment(sketch, "E28.4.1.9", {"start": v(122.54, 45.23) * mm, "end": v(132.77, 45.23) * mm});
            skLineSegment(sketch, "E28.4.2.0", {"start": v(119.39, 5.59) * mm, "end": v(116.22, -4.14) * mm});
            skLineSegment(sketch, "E28.4.2.1", {"start": v(127.64, -19.9) * mm, "end": v(124.5, -10.16) * mm});
            skLineSegment(sketch, "E28.4.2.2", {"start": v(127.64, -19.9) * mm, "end": v(119.37, -13.87) * mm});
            skLineSegment(sketch, "E28.4.2.3", {"start": v(105.99, -4.13) * mm, "end": v(116.22, -4.14) * mm});
            skLineSegment(sketch, "E28.4.2.4", {"start": v(132.77, -4.15) * mm, "end": v(124.5, -10.16) * mm});
            skLineSegment(sketch, "E28.4.2.5", {"start": v(114.26, -10.15) * mm, "end": v(111.1, -19.88) * mm});
            skLineSegment(sketch, "E28.4.2.6", {"start": v(114.26, -10.15) * mm, "end": v(105.99, -4.13) * mm});
            skLineSegment(sketch, "E28.4.2.7", {"start": v(119.37, -13.87) * mm, "end": v(111.1, -19.88) * mm});
            skLineSegment(sketch, "E28.4.2.8", {"start": v(122.54, -4.14) * mm, "end": v(119.39, 5.59) * mm});
            skLineSegment(sketch, "E28.4.2.9", {"start": v(122.54, -4.14) * mm, "end": v(132.77, -4.15) * mm});
            skLineSegment(sketch, "E28.4.3.0", {"start": v(119.39, -43.79) * mm, "end": v(116.22, -53.52) * mm});
            skLineSegment(sketch, "E28.4.3.1", {"start": v(127.64, -69.27) * mm, "end": v(124.5, -59.54) * mm});
            skLineSegment(sketch, "E28.4.3.2", {"start": v(127.64, -69.27) * mm, "end": v(119.37, -63.25) * mm});
            skLineSegment(sketch, "E28.4.3.3", {"start": v(105.99, -53.5) * mm, "end": v(116.22, -53.52) * mm});
            skLineSegment(sketch, "E28.4.3.4", {"start": v(132.77, -53.53) * mm, "end": v(124.5, -59.54) * mm});
            skLineSegment(sketch, "E28.4.3.5", {"start": v(114.26, -59.53) * mm, "end": v(111.1, -69.26) * mm});
            skLineSegment(sketch, "E28.4.3.6", {"start": v(114.26, -59.53) * mm, "end": v(105.99, -53.5) * mm});
            skLineSegment(sketch, "E28.4.3.7", {"start": v(119.37, -63.25) * mm, "end": v(111.1, -69.26) * mm});
            skLineSegment(sketch, "E28.4.3.8", {"start": v(122.54, -53.52) * mm, "end": v(119.39, -43.79) * mm});
            skLineSegment(sketch, "E28.4.3.9", {"start": v(122.54, -53.52) * mm, "end": v(132.77, -53.53) * mm});
            skLineSegment(sketch, "E28.direction1", {"start": v(-119.34, 78.88) * mm, "end": v(-61.73, 78.88) * mm, "construction": true});
            skLineSegment(sketch, "E28.direction2", {"start": v(-119.34, 78.88) * mm, "end": v(-119.34, 29.5) * mm, "construction": true});
            skSolve(sketch);
        }
        {
            var Q0;
            Q0 = qSketchRegion(id + "F2", true);
            extrude(context, id + "F3", {"entities" : qUnion([Q0]), "depth" : 0.64 * mm});
        }
        {
            var Q0;
            Q0=makeQuery(id+"F0.imprint","IMPRINT",FACE,{"disambiguationData":[TD([[makeQuery(id+"F0.imprint","IMPRINT",EDGE,{"derivedFrom":sQuery(id+"F0.wireOp",EDGE,"E0.bottom")}),-1.0]])]});
            extrude(context, id + "F4", {"entities" : qUnion([Q0]), "oppositeDirection" : true, "depth" : 5.08 * mm});
        }
    });
